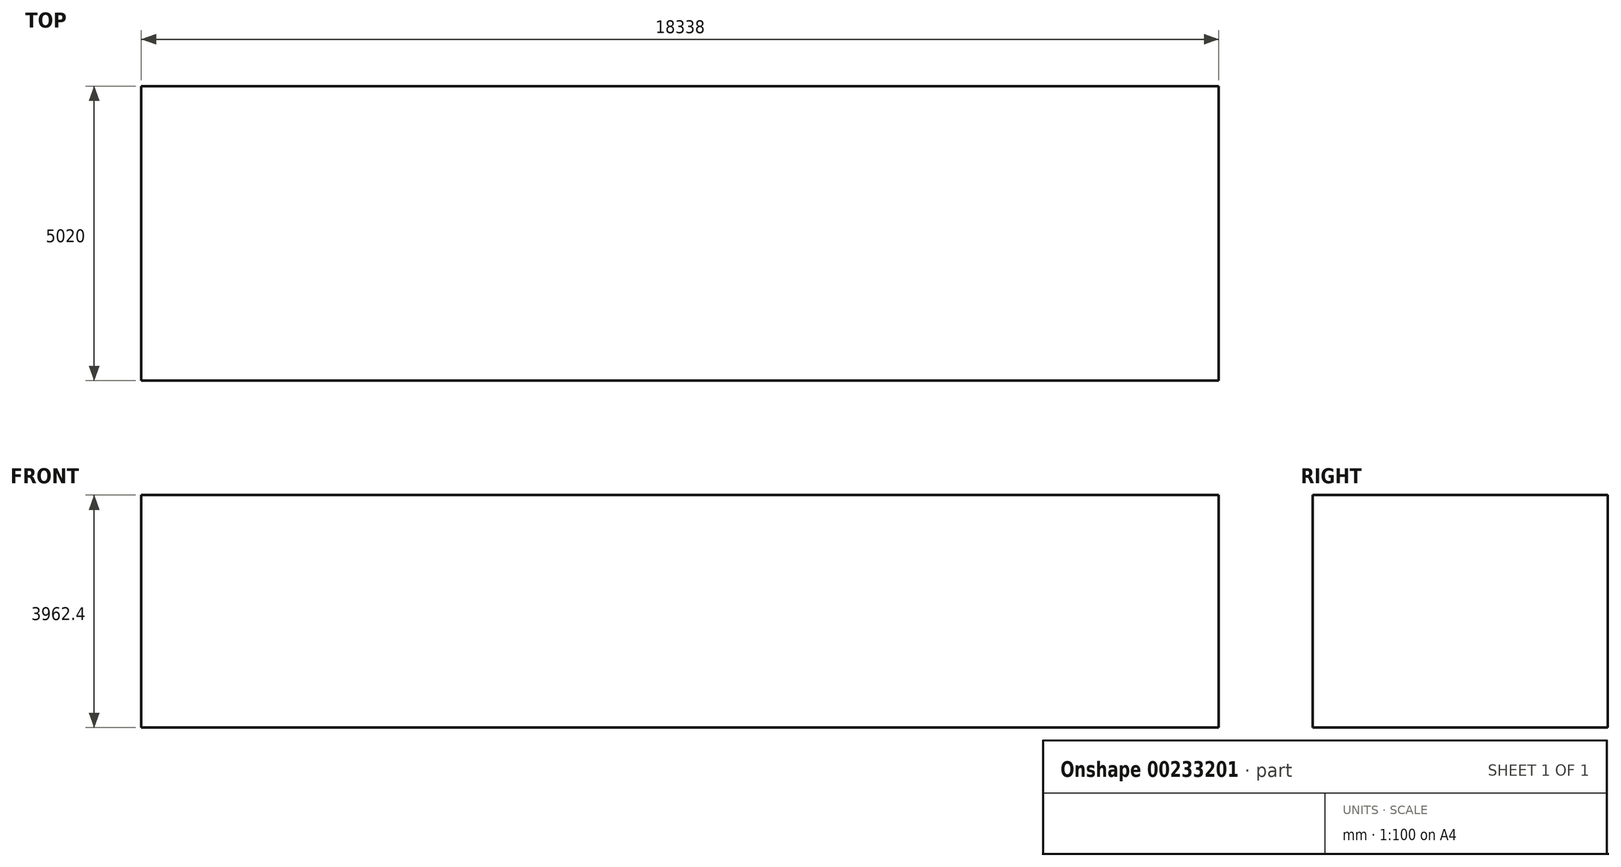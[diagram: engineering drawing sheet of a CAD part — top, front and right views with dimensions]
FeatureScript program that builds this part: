
annotation { "Feature Type Name" : "Feature", "Feature Type Description" : "" }
export const myFeature = defineFeature(function(context is Context, id is Id, definition is map)
    precondition{}
    {
        {
            var Q0;
            Q0=qCreatedBy(makeId("Top.planeOp"),FACE);
            var sketch = newSketch(context, id + "F0", { "sketchPlane" : qUnion([Q0])});
            skLineSegment(sketch, "E0.bottom", {"start": v(-9189.28, 1644.53) * mm, "end": v(9148.72, 1644.53) * mm});
            skLineSegment(sketch, "E0.top", {"start": v(-9189.28, -3375.47) * mm, "end": v(9148.72, -3375.47) * mm});
            skLineSegment(sketch, "E0.left", {"start": v(-9189.28, 1644.53) * mm, "end": v(-9189.28, -3375.47) * mm});
            skLineSegment(sketch, "E0.right", {"start": v(9148.72, 1644.53) * mm, "end": v(9148.72, -3375.47) * mm});
            skSolve(sketch);
        }
        {
            var Q0;
            Q0 = qSketchRegion(id + "F0", true);
            extrude(context, id + "F1", {"entities" : qUnion([Q0]), "depth" : 3962.4 * mm});
        }
    });
